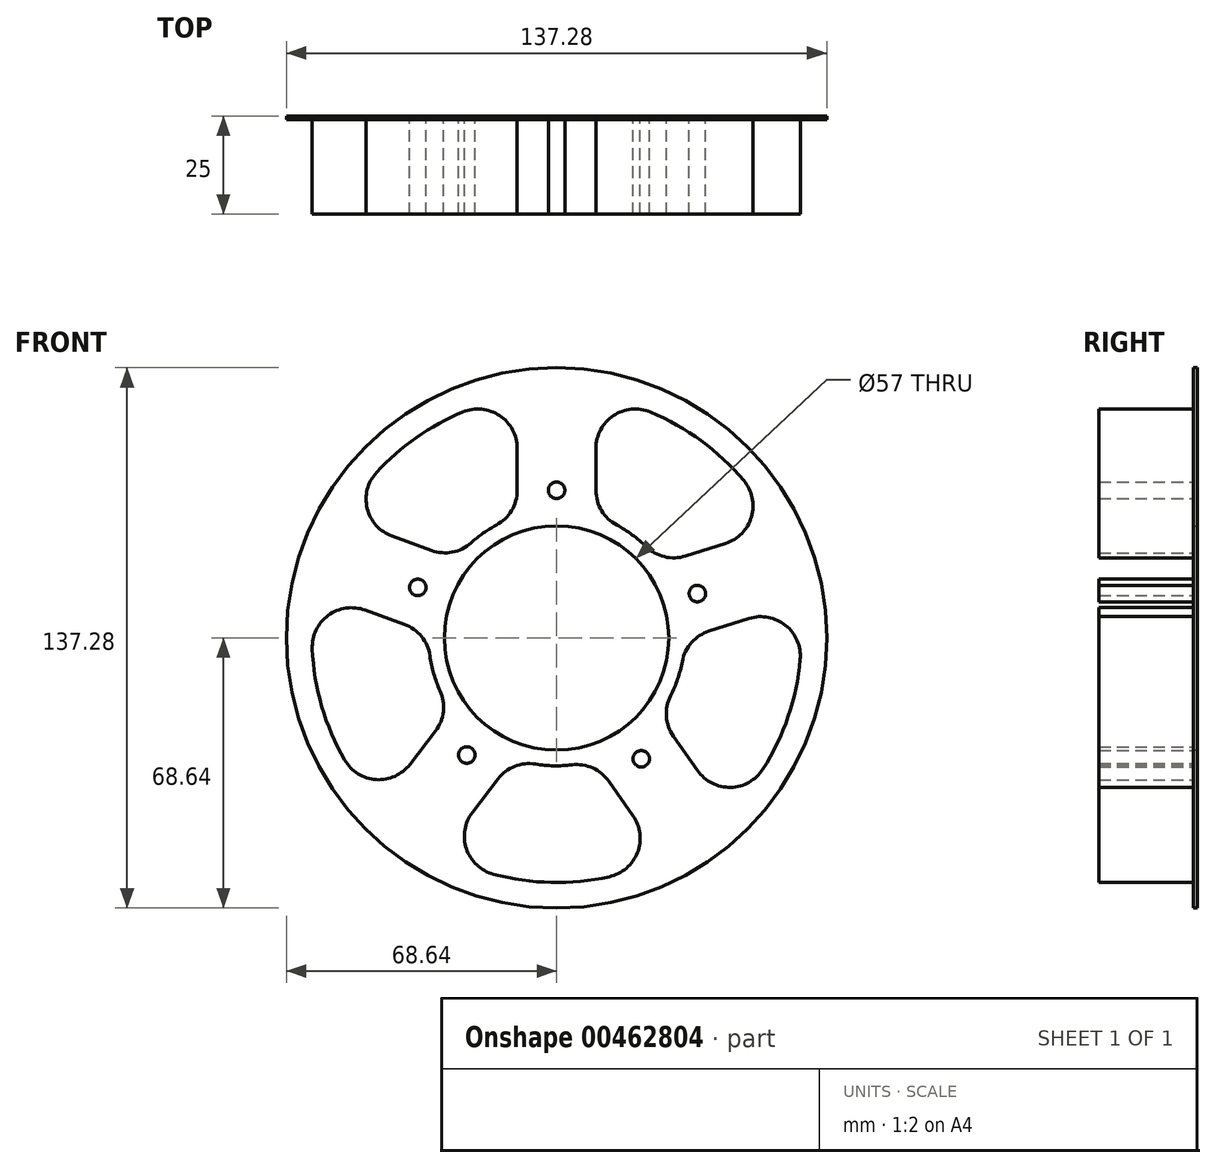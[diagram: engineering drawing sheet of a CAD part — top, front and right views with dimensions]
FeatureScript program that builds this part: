
annotation { "Feature Type Name" : "Feature", "Feature Type Description" : "" }
export const myFeature = defineFeature(function(context is Context, id is Id, definition is map)
    precondition{}
    {
        {
            var Q0;
            Q0=qCreatedBy(makeId("Front.planeOp"),FACE);
            var sketch = newSketch(context, id + "F0", { "sketchPlane" : qUnion([Q0])});
            skCircle(sketch, "E0", {"center": v(0, 0) * mm, "radius": 68.64 * mm});
            skCircle(sketch, "E1", {"center": v(0, 0) * mm, "radius": 28.5 * mm});
            skCircle(sketch, "E2", {"center": v(0, 37.5) * mm, "radius": 2.1 * mm});
            skLineSegment(sketch, "E3.0", {"start": v(10, 30.92) * mm, "end": v(10, 61.33) * mm});
            skLineSegment(sketch, "E4.0", {"start": v(-10, 30.92) * mm, "end": v(-10, 61.33) * mm});
            skPoint(sketch, "E5.start.orphan", {"position": v(0, 28.5) * mm});
            skLineSegment(sketch, "E6.1.0", {"start": v(26.49, 18.84) * mm, "end": v(55.48, 27.98) * mm});
            skLineSegment(sketch, "E6.1.1", {"start": v(32.5, -0.24) * mm, "end": v(61.5, 8.9) * mm});
            skCircle(sketch, "E6.1.4", {"center": v(35.76, 11.28) * mm, "radius": 2.1 * mm});
            skLineSegment(sketch, "E6.2.0", {"start": v(25.93, -19.6) * mm, "end": v(43.37, -44.5) * mm});
            skLineSegment(sketch, "E6.2.1", {"start": v(9.55, -31.07) * mm, "end": v(26.98, -55.97) * mm});
            skCircle(sketch, "E6.2.4", {"center": v(21.5, -30.72) * mm, "radius": 2.1 * mm});
            skLineSegment(sketch, "E6.3.0", {"start": v(-10.9, -30.62) * mm, "end": v(-29.4, -54.74) * mm});
            skLineSegment(sketch, "E6.3.1", {"start": v(-26.76, -18.45) * mm, "end": v(-45.27, -42.56) * mm});
            skCircle(sketch, "E6.3.4", {"center": v(-22.83, -29.75) * mm, "radius": 2.1 * mm});
            skLineSegment(sketch, "E6.4.0", {"start": v(-32.48, 1.18) * mm, "end": v(-61.05, 11.58) * mm});
            skLineSegment(sketch, "E6.4.1", {"start": v(-25.64, 19.97) * mm, "end": v(-54.2, 30.37) * mm});
            skCircle(sketch, "E6.4.4", {"center": v(-35.24, 12.83) * mm, "radius": 2.1 * mm});
            skLineSegment(sketch, "E6.anchor1", {"start": v(0, 0) * mm, "end": v(-10, 28.5) * mm, "construction": true});
            skLineSegment(sketch, "E6.anchor2", {"start": v(0, 0) * mm, "end": v(-30.2, 0.35) * mm, "construction": true});
            skCircle(sketch, "E7", {"center": v(0, 0) * mm, "radius": 32.5 * mm});
            skArc(sketch, "E8", {"start": v(-10, 61.33) * mm, "mid": v(-35.64, 50.9) * mm, "end": v(-54.2, 30.37) * mm});
            skPoint(sketch, "E9.orphan", {"position": v(8.16, -29.08) * mm});
            skPoint(sketch, "E10.orphan", {"position": v(-25.28, -16.52) * mm});
            skPoint(sketch, "E11.orphan", {"position": v(-10, 67.9) * mm});
            skPoint(sketch, "E12.orphan", {"position": v(10, 67.9) * mm});
            skArc(sketch, "E13.trimOffspring", {"start": v(-61.05, 11.58) * mm, "mid": v(-59.65, -17.39) * mm, "end": v(-45.27, -42.56) * mm});
            skPoint(sketch, "E14.orphan", {"position": v(-67.23, 13.83) * mm});
            skPoint(sketch, "E15.orphan", {"position": v(-60.39, 32.62) * mm});
            skArc(sketch, "E16.trimOffspring", {"start": v(-29.4, -54.74) * mm, "mid": v(-1.36, -62.12) * mm, "end": v(26.98, -55.97) * mm});
            skPoint(sketch, "E17.orphan", {"position": v(-33.4, -59.96) * mm});
            skPoint(sketch, "E18.orphan", {"position": v(-49.27, -47.78) * mm});
            skArc(sketch, "E19.trimOffspring", {"start": v(43.37, -44.5) * mm, "mid": v(58.84, -19.97) * mm, "end": v(61.5, 8.9) * mm});
            skPoint(sketch, "E20.orphan", {"position": v(30.76, -61.36) * mm});
            skPoint(sketch, "E21.orphan", {"position": v(47.14, -49.89) * mm});
            skArc(sketch, "E22.trimOffspring", {"start": v(55.48, 27.98) * mm, "mid": v(36.74, 50.1) * mm, "end": v(10, 61.33) * mm});
            skPoint(sketch, "E23.orphan", {"position": v(61.75, 29.96) * mm});
            skPoint(sketch, "E24.orphan", {"position": v(67.77, 10.88) * mm});
            skSolve(sketch);
        }
        {
            var Q0;
            Q0=makeQuery(id+"F0.imprint","IMPRINT",FACE,{"disambiguationData":[TD([[makeQuery(id+"F0.imprint","IMPRINT",EDGE,{"derivedFrom":sQuery(id+"F0.wireOp",EDGE,"E0")}),1.0]])]});
            var Q1;
            {var subQ0=sQuery(id+"F0.wireOp",EDGE,"E3.0");Q1=makeQuery(id+"F0.imprint","IMPRINT",FACE,{"disambiguationData":[TD([[makeQuery(id+"F0.imprint","IMPRINT",EDGE,{"derivedFrom":subQ0}),-1.0]])]});}
            var Q2;
            {var subQ0=sQuery(id+"F0.wireOp",EDGE,"E4.0");Q2=makeQuery(id+"F0.imprint","IMPRINT",FACE,{"disambiguationData":[TD([[makeQuery(id+"F0.imprint","IMPRINT",EDGE,{"derivedFrom":subQ0}),1.0]])]});}
            var Q3;
            Q3=makeQuery(id+"F0.imprint","IMPRINT",FACE,{"disambiguationData":[TD([[makeQuery(id+"F0.imprint","IMPRINT",EDGE,{"derivedFrom":sQuery(id+"F0.wireOp",EDGE,"E2")}),1.0]])]});
            var Q4;
            Q4=makeQuery(id+"F0.imprint","IMPRINT",FACE,{"disambiguationData":[TD([[makeQuery(id+"F0.imprint","IMPRINT",EDGE,{"derivedFrom":sQuery(id+"F0.wireOp",EDGE,"E6.1.4")}),1.0]])]});
            var Q5;
            {var subQ0=sQuery(id+"F0.wireOp",EDGE,"E6.1.1");Q5=makeQuery(id+"F0.imprint","IMPRINT",FACE,{"disambiguationData":[TD([[makeQuery(id+"F0.imprint","IMPRINT",EDGE,{"derivedFrom":subQ0}),-1.0]])]});}
            var Q6;
            {var subQ0=sQuery(id+"F0.wireOp",EDGE,"E6.2.1");Q6=makeQuery(id+"F0.imprint","IMPRINT",FACE,{"disambiguationData":[TD([[makeQuery(id+"F0.imprint","IMPRINT",EDGE,{"derivedFrom":subQ0}),-1.0]])]});}
            var Q7;
            {var subQ0=sQuery(id+"F0.wireOp",EDGE,"E6.3.1");Q7=makeQuery(id+"F0.imprint","IMPRINT",FACE,{"disambiguationData":[TD([[makeQuery(id+"F0.imprint","IMPRINT",EDGE,{"derivedFrom":subQ0}),-1.0]])]});}
            var Q8;
            Q8=makeQuery(id+"F0.imprint","IMPRINT",FACE,{"disambiguationData":[TD([[makeQuery(id+"F0.imprint","IMPRINT",EDGE,{"derivedFrom":sQuery(id+"F0.wireOp",EDGE,"E6.4.4")}),1.0]])]});
            var Q9;
            Q9=makeQuery(id+"F0.imprint","IMPRINT",FACE,{"disambiguationData":[TD([[makeQuery(id+"F0.imprint","IMPRINT",EDGE,{"derivedFrom":sQuery(id+"F0.wireOp",EDGE,"E1")}),-1.0]])]});
            var Q10;
            Q10=makeQuery(id+"F0.imprint","IMPRINT",FACE,{"disambiguationData":[TD([[makeQuery(id+"F0.imprint","IMPRINT",EDGE,{"derivedFrom":sQuery(id+"F0.wireOp",EDGE,"E6.2.4")}),1.0]])]});
            var Q11;
            Q11=makeQuery(id+"F0.imprint","IMPRINT",FACE,{"disambiguationData":[TD([[makeQuery(id+"F0.imprint","IMPRINT",EDGE,{"derivedFrom":sQuery(id+"F0.wireOp",EDGE,"E6.3.4")}),1.0]])]});
            extrude(context, id + "F1", {"entities" : qUnion([Q0, Q1, Q2, Q3, Q4, Q5, Q6, Q7, Q8, Q9, Q10, Q11]), "depth" : 1 * mm});
        }
        {
            var Q0;
            {var subQ0=sQuery(id+"F0.wireOp",EDGE,"E3.0");Q0=makeQuery(id+"F0.imprint","IMPRINT",FACE,{"disambiguationData":[TD([[makeQuery(id+"F0.imprint","IMPRINT",EDGE,{"derivedFrom":subQ0}),-1.0]])]});}
            var Q1;
            {var subQ0=sQuery(id+"F0.wireOp",EDGE,"E4.0");Q1=makeQuery(id+"F0.imprint","IMPRINT",FACE,{"disambiguationData":[TD([[makeQuery(id+"F0.imprint","IMPRINT",EDGE,{"derivedFrom":subQ0}),1.0]])]});}
            var Q2;
            {var subQ0=sQuery(id+"F0.wireOp",EDGE,"E6.3.1");Q2=makeQuery(id+"F0.imprint","IMPRINT",FACE,{"disambiguationData":[TD([[makeQuery(id+"F0.imprint","IMPRINT",EDGE,{"derivedFrom":subQ0}),-1.0]])]});}
            var Q3;
            {var subQ0=sQuery(id+"F0.wireOp",EDGE,"E6.2.1");Q3=makeQuery(id+"F0.imprint","IMPRINT",FACE,{"disambiguationData":[TD([[makeQuery(id+"F0.imprint","IMPRINT",EDGE,{"derivedFrom":subQ0}),-1.0]])]});}
            var Q4;
            {var subQ0=sQuery(id+"F0.wireOp",EDGE,"E6.1.1");Q4=makeQuery(id+"F0.imprint","IMPRINT",FACE,{"disambiguationData":[TD([[makeQuery(id+"F0.imprint","IMPRINT",EDGE,{"derivedFrom":subQ0}),-1.0]])]});}
            var Q5;
            Q5=makeQuery(id+"F0.imprint","IMPRINT",FACE,{"disambiguationData":[TD([[makeQuery(id+"F0.imprint","IMPRINT",EDGE,{"derivedFrom":sQuery(id+"F0.wireOp",EDGE,"E6.1.4")}),1.0]])]});
            var Q6;
            Q6=makeQuery(id+"F0.imprint","IMPRINT",FACE,{"disambiguationData":[TD([[makeQuery(id+"F0.imprint","IMPRINT",EDGE,{"derivedFrom":sQuery(id+"F0.wireOp",EDGE,"E6.2.4")}),1.0]])]});
            var Q7;
            Q7=makeQuery(id+"F0.imprint","IMPRINT",FACE,{"disambiguationData":[TD([[makeQuery(id+"F0.imprint","IMPRINT",EDGE,{"derivedFrom":sQuery(id+"F0.wireOp",EDGE,"E6.3.4")}),1.0]])]});
            var Q8;
            Q8=makeQuery(id+"F0.imprint","IMPRINT",FACE,{"disambiguationData":[TD([[makeQuery(id+"F0.imprint","IMPRINT",EDGE,{"derivedFrom":sQuery(id+"F0.wireOp",EDGE,"E6.4.4")}),1.0]])]});
            var Q9;
            Q9=makeQuery(id+"F0.imprint","IMPRINT",FACE,{"disambiguationData":[TD([[makeQuery(id+"F0.imprint","IMPRINT",EDGE,{"derivedFrom":sQuery(id+"F0.wireOp",EDGE,"E2")}),1.0]])]});
            extrude(context, id + "F2", {"entities" : qUnion([Q0, Q1, Q2, Q3, Q4, Q5, Q6, Q7, Q8, Q9]), "operationType" : NewBodyOperationType.ADD, "depth" : 25 * mm});
        }
        {
            var Q0;
            Q0=makeQuery(id+"F2.opExtrude","SWEPT_EDGE",EDGE,{"disambiguationData":[OSD([sQuery(id+"F0.wireOp",EDGE,"E6.4.1"),sQuery(id+"F0.wireOp",EDGE,"E8")])]});
            var Q1;
            Q1=makeQuery(id+"F2.opExtrude","SWEPT_EDGE",EDGE,{"disambiguationData":[OSD([sQuery(id+"F0.wireOp",EDGE,"E6.4.1"),sQuery(id+"F0.wireOp",EDGE,"E7")])]});
            var Q2;
            Q2=makeQuery(id+"F2.opExtrude","SWEPT_EDGE",EDGE,{"disambiguationData":[OSD([sQuery(id+"F0.wireOp",EDGE,"E4.0"),sQuery(id+"F0.wireOp",EDGE,"E7")])]});
            var Q3;
            Q3=makeQuery(id+"F2.opExtrude","SWEPT_EDGE",EDGE,{"disambiguationData":[OSD([sQuery(id+"F0.wireOp",EDGE,"E4.0"),sQuery(id+"F0.wireOp",EDGE,"E8")])]});
            var Q4;
            Q4=makeQuery(id+"F2.opExtrude","SWEPT_EDGE",EDGE,{"disambiguationData":[OSD([sQuery(id+"F0.wireOp",EDGE,"E6.4.0"),sQuery(id+"F0.wireOp",EDGE,"E7")])]});
            var Q5;
            Q5=makeQuery(id+"F2.opExtrude","SWEPT_EDGE",EDGE,{"disambiguationData":[OSD([sQuery(id+"F0.wireOp",EDGE,"E6.3.1"),sQuery(id+"F0.wireOp",EDGE,"E7")])]});
            var Q6;
            Q6=makeQuery(id+"F2.opExtrude","SWEPT_EDGE",EDGE,{"disambiguationData":[OSD([sQuery(id+"F0.wireOp",EDGE,"E6.4.0"),sQuery(id+"F0.wireOp",EDGE,"E13.trimOffspring")])]});
            var Q7;
            Q7=makeQuery(id+"F2.opExtrude","SWEPT_EDGE",EDGE,{"disambiguationData":[OSD([sQuery(id+"F0.wireOp",EDGE,"E6.3.1"),sQuery(id+"F0.wireOp",EDGE,"E13.trimOffspring")])]});
            var Q8;
            Q8=makeQuery(id+"F2.opExtrude","SWEPT_EDGE",EDGE,{"disambiguationData":[OSD([sQuery(id+"F0.wireOp",EDGE,"E6.3.0"),sQuery(id+"F0.wireOp",EDGE,"E16.trimOffspring")])]});
            var Q9;
            Q9=makeQuery(id+"F2.opExtrude","SWEPT_EDGE",EDGE,{"disambiguationData":[OSD([sQuery(id+"F0.wireOp",EDGE,"E6.2.1"),sQuery(id+"F0.wireOp",EDGE,"E16.trimOffspring")])]});
            var Q10;
            Q10=makeQuery(id+"F2.opExtrude","SWEPT_EDGE",EDGE,{"disambiguationData":[OSD([sQuery(id+"F0.wireOp",EDGE,"E6.2.1"),sQuery(id+"F0.wireOp",EDGE,"E7")])]});
            var Q11;
            Q11=makeQuery(id+"F2.opExtrude","SWEPT_EDGE",EDGE,{"disambiguationData":[OSD([sQuery(id+"F0.wireOp",EDGE,"E6.3.0"),sQuery(id+"F0.wireOp",EDGE,"E7")])]});
            var Q12;
            Q12=makeQuery(id+"F2.opExtrude","SWEPT_EDGE",EDGE,{"disambiguationData":[OSD([sQuery(id+"F0.wireOp",EDGE,"E6.1.1"),sQuery(id+"F0.wireOp",EDGE,"E7")])]});
            var Q13;
            Q13=makeQuery(id+"F2.opExtrude","SWEPT_EDGE",EDGE,{"disambiguationData":[OSD([sQuery(id+"F0.wireOp",EDGE,"E6.2.0"),sQuery(id+"F0.wireOp",EDGE,"E7")])]});
            var Q14;
            Q14=makeQuery(id+"F2.opExtrude","SWEPT_EDGE",EDGE,{"disambiguationData":[OSD([sQuery(id+"F0.wireOp",EDGE,"E6.2.0"),sQuery(id+"F0.wireOp",EDGE,"E19.trimOffspring")])]});
            var Q15;
            Q15=makeQuery(id+"F2.opExtrude","SWEPT_EDGE",EDGE,{"disambiguationData":[OSD([sQuery(id+"F0.wireOp",EDGE,"E6.1.1"),sQuery(id+"F0.wireOp",EDGE,"E19.trimOffspring")])]});
            var Q16;
            Q16=makeQuery(id+"F2.opExtrude","SWEPT_EDGE",EDGE,{"disambiguationData":[OSD([sQuery(id+"F0.wireOp",EDGE,"E6.1.0"),sQuery(id+"F0.wireOp",EDGE,"E22.trimOffspring")])]});
            var Q17;
            Q17=makeQuery(id+"F2.opExtrude","SWEPT_EDGE",EDGE,{"disambiguationData":[OSD([sQuery(id+"F0.wireOp",EDGE,"E3.0"),sQuery(id+"F0.wireOp",EDGE,"E22.trimOffspring")])]});
            var Q18;
            Q18=makeQuery(id+"F2.opExtrude","SWEPT_EDGE",EDGE,{"disambiguationData":[OSD([sQuery(id+"F0.wireOp",EDGE,"E3.0"),sQuery(id+"F0.wireOp",EDGE,"E7")])]});
            var Q19;
            Q19=makeQuery(id+"F2.opExtrude","SWEPT_EDGE",EDGE,{"disambiguationData":[OSD([sQuery(id+"F0.wireOp",EDGE,"E6.1.0"),sQuery(id+"F0.wireOp",EDGE,"E7")])]});
            fillet(context, id + "F3", {"entities" : qUnion([Q0, Q1, Q2, Q3, Q4, Q5, Q6, Q7, Q8, Q9, Q10, Q11, Q12, Q13, Q14, Q15, Q16, Q17, Q18, Q19]), "radius" : 10 * mm, "tangentPropagation" : true, "allowEdgeOverflow" : false});
        }
    });
